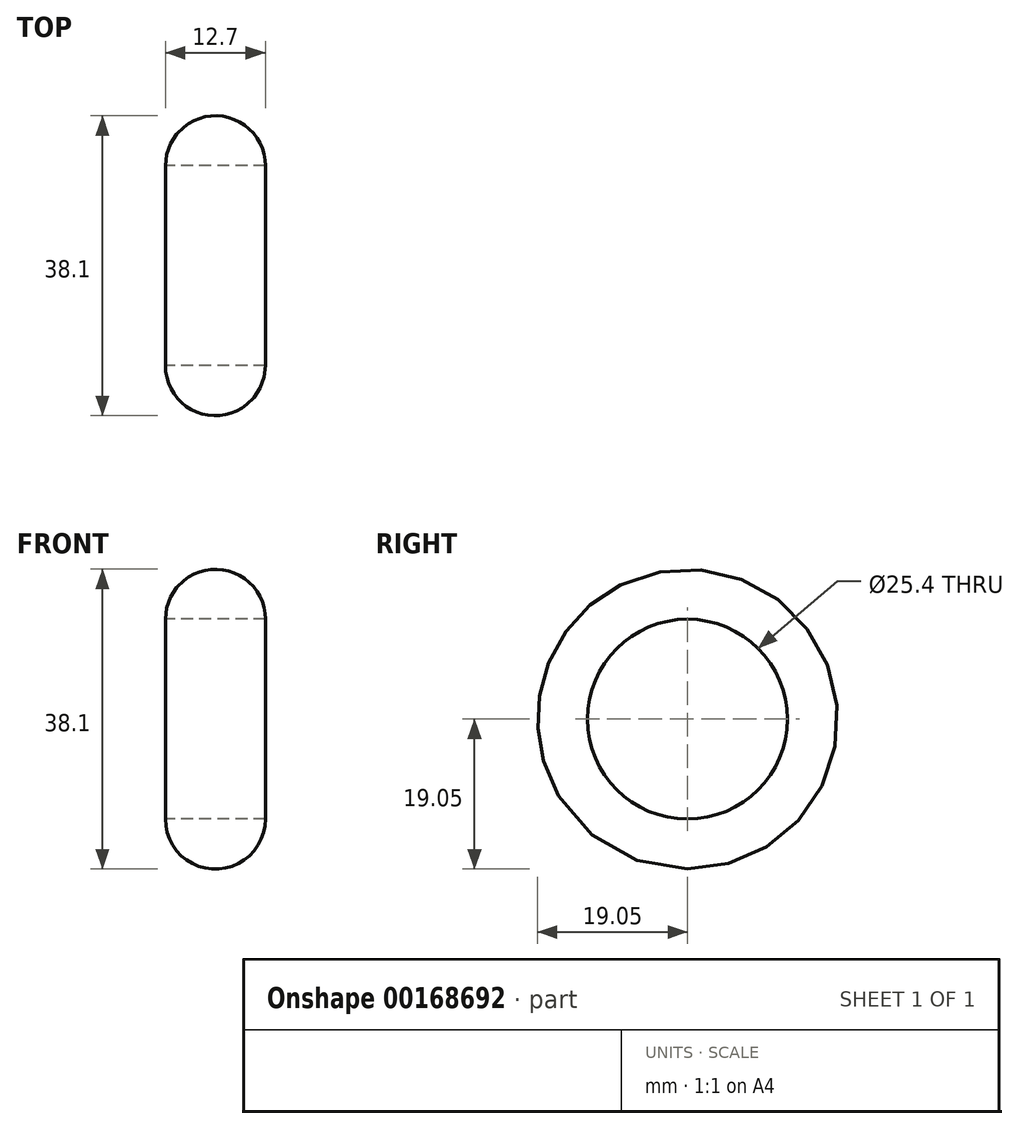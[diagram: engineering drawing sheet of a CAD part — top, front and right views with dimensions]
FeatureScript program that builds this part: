
annotation { "Feature Type Name" : "Feature", "Feature Type Description" : "" }
export const myFeature = defineFeature(function(context is Context, id is Id, definition is map)
    precondition{}
    {
        {
            var Q0;
            Q0=qCreatedBy(makeId("Right.planeOp"),FACE);
            var sketch = newSketch(context, id + "F0", { "sketchPlane" : qUnion([Q0])});
            skCircle(sketch, "E0", {"center": v(0, 0) * mm, "radius": 19.05 * mm});
            skCircle(sketch, "E1.0", {"center": v(0, 0) * mm, "radius": 12.7 * mm});
            skSolve(sketch);
        }
        {
            var Q0;
            Q0=makeQuery(id+"F0.imprint","IMPRINT",FACE,{"disambiguationData":[TD([[makeQuery(id+"F0.imprint","IMPRINT",EDGE,{"derivedFrom":sQuery(id+"F0.wireOp",EDGE,"E0")}),1.0]])]});
            extrude(context, id + "F1", {"entities" : qUnion([Q0]), "depth" : 12.7 * mm});
        }
        {
            var Q0;
            Q0=makeQuery(id+"F1.opExtrude","CAP_EDGE",EDGE,{"disambiguationData":[OSD([sQuery(id+"F0.wireOp",EDGE,"E0")])],"isStart":false});
            var Q1;
            Q1=makeQuery(id+"F1.opExtrude","CAP_EDGE",EDGE,{"disambiguationData":[OSD([sQuery(id+"F0.wireOp",EDGE,"E0")])],"isStart":true});
            fillet(context, id + "F2", {"entities" : qUnion([Q0, Q1]), "radius" : 6.35 * mm, "tangentPropagation" : true, "allowEdgeOverflow" : false});
        }
    });
